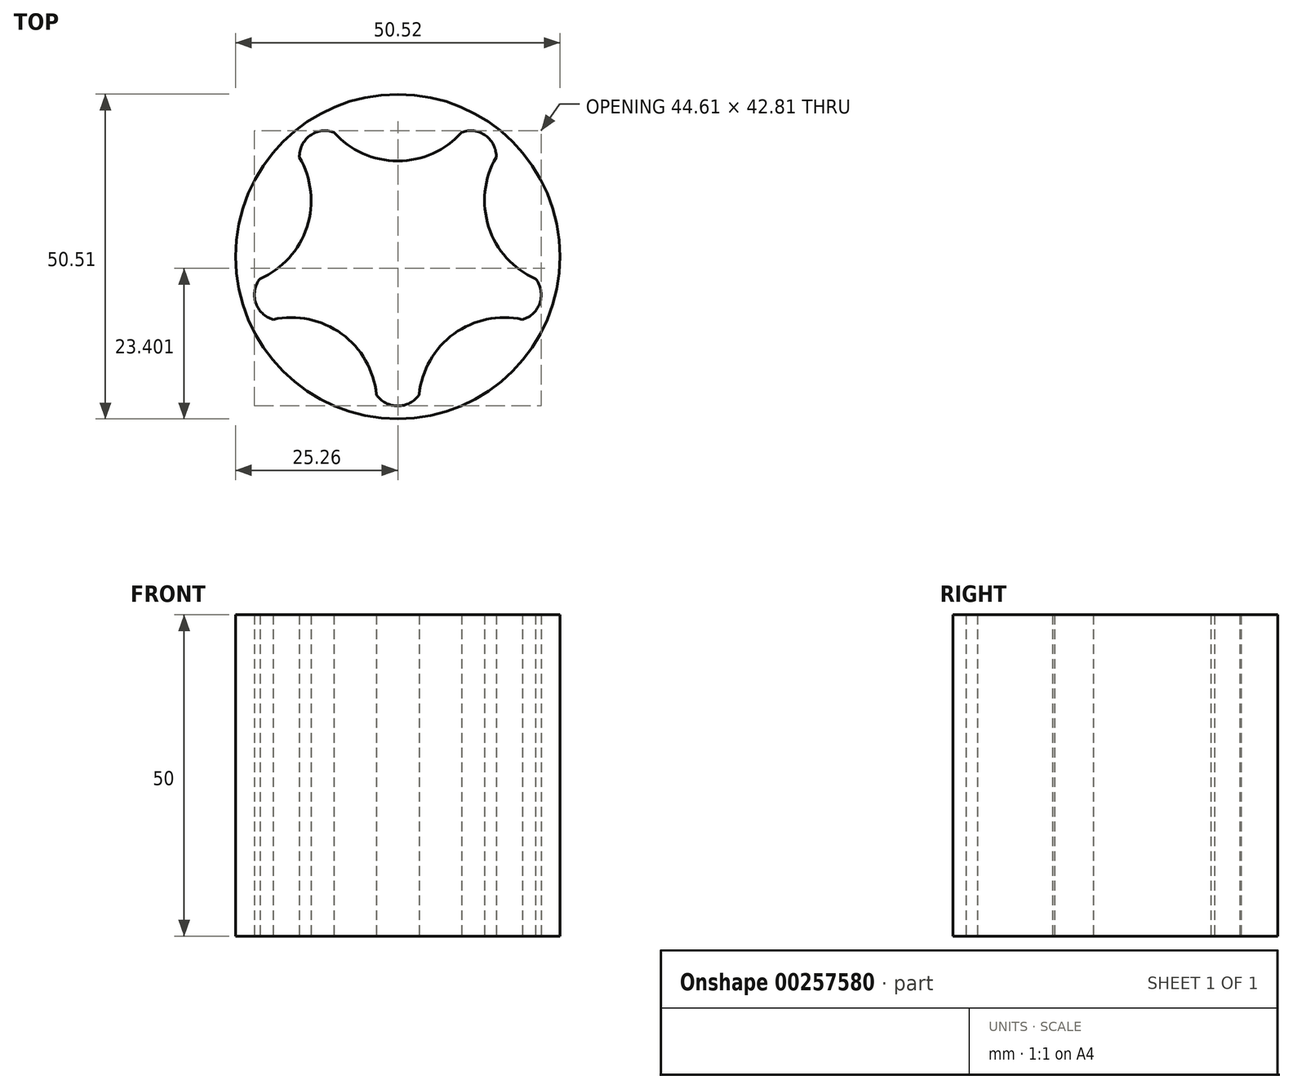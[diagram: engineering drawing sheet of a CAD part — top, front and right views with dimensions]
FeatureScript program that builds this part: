
annotation { "Feature Type Name" : "Feature", "Feature Type Description" : "" }
export const myFeature = defineFeature(function(context is Context, id is Id, definition is map)
    precondition{}
    {
        {
            var Q0;
            Q0=qCreatedBy(makeId("Top.planeOp"),FACE);
            var sketch = newSketch(context, id + "F0", { "sketchPlane" : qUnion([Q0])});
            skPoint(sketch, "E0", {"position": v(0, 16.5) * mm});
            skArc(sketch, "E1", {"start": v(3.5, 16.5) * mm, "mid": v(7.95, 7.95) * mm, "end": v(16.5, 3.5) * mm});
            skArc(sketch, "E2.MirrorCS", {"start": v(3.5, -16.5) * mm, "mid": v(7.95, -7.95) * mm, "end": v(16.5, -3.5) * mm});
            skArc(sketch, "E3.MirrorCS", {"start": v(-3.5, 16.5) * mm, "mid": v(-7.95, 7.95) * mm, "end": v(-16.5, 3.5) * mm});
            skArc(sketch, "E4.MirrorCS", {"start": v(-3.5, -16.5) * mm, "mid": v(-7.95, -7.95) * mm, "end": v(-16.5, -3.5) * mm});
            skArc(sketch, "E5", {"start": v(3.5, 16.5) * mm, "mid": v(0, 18.56) * mm, "end": v(-3.5, 16.5) * mm});
            skArc(sketch, "E6.MirrorCS", {"start": v(3.5, -16.5) * mm, "mid": v(0, -18.56) * mm, "end": v(-3.5, -16.5) * mm});
            skArc(sketch, "E7", {"start": v(16.5, -3.5) * mm, "mid": v(18.56, 0) * mm, "end": v(16.5, 3.5) * mm});
            skArc(sketch, "E8.MirrorCS", {"start": v(-16.5, -3.5) * mm, "mid": v(-18.56, 0) * mm, "end": v(-16.5, 3.5) * mm});
            skPoint(sketch, "E9", {"position": v(0, 0) * mm});
            skArc(sketch, "E10", {"start": v(14.14, 16.52) * mm, "mid": v(11.24, 7.33) * mm, "end": v(14.14, -1.87) * mm});
            skArc(sketch, "E11.MirrorCS", {"start": v(-9.2, -6.82) * mm, "mid": v(0, -3.91) * mm, "end": v(9.2, -6.82) * mm});
            skArc(sketch, "E12.MirrorCS", {"start": v(9.2, 21.47) * mm, "mid": v(0, 18.56) * mm, "end": v(-9.2, 21.47) * mm});
            skArc(sketch, "E13.MirrorCS", {"start": v(-14.14, -1.87) * mm, "mid": v(-11.24, 7.33) * mm, "end": v(-14.14, 16.52) * mm});
            skArc(sketch, "E14", {"start": v(14.14, 16.52) * mm, "mid": v(13.13, 20.45) * mm, "end": v(9.2, 21.47) * mm});
            skArc(sketch, "E15.MirrorCS", {"start": v(-9.2, -6.82) * mm, "mid": v(-13.13, -5.8) * mm, "end": v(-14.14, -1.87) * mm});
            skArc(sketch, "E16", {"start": v(9.2, -6.82) * mm, "mid": v(13.13, -5.8) * mm, "end": v(14.14, -1.87) * mm});
            skArc(sketch, "E17.MirrorCS", {"start": v(-14.14, 16.52) * mm, "mid": v(-13.13, 20.45) * mm, "end": v(-9.2, 21.47) * mm});
            skPoint(sketch, "E18", {"position": v(0, 7.33) * mm});
            skSolve(sketch);
        }
        {
            var Q0;
            Q0=makeQuery(id+"F0.imprint","IMPRINT",FACE,{"disambiguationData":[TD([[makeQuery(id+"F0.imprint","IMPRINT",EDGE,{"derivedFrom":sQuery(id+"F0.wireOp",EDGE,"E1")}),-1.0]])]});
            extrude(context, id + "F1", {"entities" : qUnion([Q0]), "depth" : 1 * mm});
        }
        {
            var Q0;
            Q0 = qSketchRegion(id + "F0", true);
            extrude(context, id + "F2", {"entities" : qUnion([Q0]), "operationType" : NewBodyOperationType.ADD, "depth" : 2 * mm});
        }
        {
            var Q0;
            Q0=makeQuery(id+"F2.opExtrude","CAP_FACE",FACE,{"disambiguationData":[OSD([sQuery(id+"F0.wireOp",EDGE,"E1"),sQuery(id+"F0.wireOp",EDGE,"E2.MirrorCS"),sQuery(id+"F0.wireOp",EDGE,"E3.MirrorCS"),sQuery(id+"F0.wireOp",EDGE,"E4.MirrorCS"),sQuery(id+"F0.wireOp",EDGE,"E6.MirrorCS"),sQuery(id+"F0.wireOp",EDGE,"E7"),sQuery(id+"F0.wireOp",EDGE,"E8.MirrorCS"),sQuery(id+"F0.wireOp",EDGE,"E10"),sQuery(id+"F0.wireOp",EDGE,"E12.MirrorCS"),sQuery(id+"F0.wireOp",EDGE,"E13.MirrorCS"),sQuery(id+"F0.wireOp",EDGE,"E14"),sQuery(id+"F0.wireOp",EDGE,"E15.MirrorCS"),sQuery(id+"F0.wireOp",EDGE,"E16"),sQuery(id+"F0.wireOp",EDGE,"E17.MirrorCS")])],"isStart":false});
            var sketch = newSketch(context, id + "F3", { "sketchPlane" : qUnion([Q0])});
            skArc(sketch, "E19", {"start": v(-9.93, 23.02) * mm, "mid": v(0, 18.56) * mm, "end": v(9.93, 23.02) * mm});
            skArc(sketch, "E20.1.0", {"start": v(15.31, 19.1) * mm, "mid": v(14.14, 8.29) * mm, "end": v(21.45, 0.22) * mm});
            skArc(sketch, "E20.2.0", {"start": v(19.4, -6.11) * mm, "mid": v(8.74, -8.34) * mm, "end": v(3.33, -17.78) * mm});
            skArc(sketch, "E20.3.0", {"start": v(-3.33, -17.78) * mm, "mid": v(-8.74, -8.34) * mm, "end": v(-19.4, -6.11) * mm});
            skArc(sketch, "E20.4.0", {"start": v(-21.45, 0.22) * mm, "mid": v(-14.14, 8.29) * mm, "end": v(-15.31, 19.1) * mm});
            skPoint(sketch, "E20.center", {"position": v(0, 3.7) * mm});
            skLineSegment(sketch, "E20.anchor1", {"start": v(0, 3.7) * mm, "end": v(0, 31.85) * mm, "construction": true});
            skLineSegment(sketch, "E20.anchor2", {"start": v(0, 3.7) * mm, "end": v(-26.78, 12.4) * mm, "construction": true});
            skArc(sketch, "E21", {"start": v(-3.33, -17.78) * mm, "mid": v(0, -19.56) * mm, "end": v(3.33, -17.78) * mm});
            skArc(sketch, "E22.1.0", {"start": v(19.4, -6.11) * mm, "mid": v(22.12, -3.5) * mm, "end": v(21.45, 0.22) * mm});
            skArc(sketch, "E22.2.0", {"start": v(15.31, 19.1) * mm, "mid": v(13.67, 22.5) * mm, "end": v(9.93, 23.02) * mm});
            skArc(sketch, "E22.3.0", {"start": v(-9.93, 23.02) * mm, "mid": v(-13.67, 22.5) * mm, "end": v(-15.31, 19.1) * mm});
            skArc(sketch, "E22.4.0", {"start": v(-21.45, 0.22) * mm, "mid": v(-22.12, -3.5) * mm, "end": v(-19.4, -6.11) * mm});
            skSolve(sketch);
        }
        {
            var Q0;
            Q0=makeQuery(id+"F3.imprint","IMPRINT",FACE,{"disambiguationData":[TD([[makeQuery(id+"F3.imprint","IMPRINT",EDGE,{"derivedFrom":sQuery(id+"F3.wireOp",EDGE,"E20.4.0")}),-1.0]])]});
            var Q1;
            Q1=makeQuery(id+"F3.imprint","IMPRINT",FACE,{"disambiguationData":[TD([[makeQuery(id+"F3.imprint","IMPRINT",EDGE,{"derivedFrom":sQuery(id+"F3.wireOp",EDGE,"E20.1.0")}),-1.0]])]});
            var Q2;
            {var subQ0=sQuery(id+"F3.wireOp",EDGE,"E21");Q2=makeQuery(id+"F3.imprint","IMPRINT",FACE,{"disambiguationData":[TD([[makeQuery(id+"F3.imprint","IMPRINT",EDGE,{"derivedFrom":subQ0}),1.0]])]});}
            var Q3;
            Q3=makeQuery(id+"F3.imprint","IMPRINT",FACE,{"disambiguationData":[TD([[makeQuery(id+"F3.imprint","IMPRINT",EDGE,{"derivedFrom":makeQuery(id+"F2.opExtrude","CAP_EDGE",EDGE,{"disambiguationData":[OSD([sQuery(id+"F0.wireOp",EDGE,"E1")])],"isStart":false})}),-1.0]])]});
            var Q4;
            Q4=makeQuery(id+"F2.opExtrude","CAP_FACE",FACE,{"disambiguationData":[OSD([sQuery(id+"F0.wireOp",EDGE,"E1"),sQuery(id+"F0.wireOp",EDGE,"E2.MirrorCS"),sQuery(id+"F0.wireOp",EDGE,"E3.MirrorCS"),sQuery(id+"F0.wireOp",EDGE,"E4.MirrorCS"),sQuery(id+"F0.wireOp",EDGE,"E6.MirrorCS"),sQuery(id+"F0.wireOp",EDGE,"E7"),sQuery(id+"F0.wireOp",EDGE,"E8.MirrorCS"),sQuery(id+"F0.wireOp",EDGE,"E10"),sQuery(id+"F0.wireOp",EDGE,"E12.MirrorCS"),sQuery(id+"F0.wireOp",EDGE,"E13.MirrorCS"),sQuery(id+"F0.wireOp",EDGE,"E14"),sQuery(id+"F0.wireOp",EDGE,"E15.MirrorCS"),sQuery(id+"F0.wireOp",EDGE,"E16"),sQuery(id+"F0.wireOp",EDGE,"E17.MirrorCS")])],"isStart":false});
            extrude(context, id + "F4", {"entities" : qUnion([Q0, Q1, Q2, Q3, Q4]), "operationType" : NewBodyOperationType.ADD, "oppositeDirection" : true, "depth" : 5 * mm, "hasSecondDirection" : true, "secondDirectionOppositeDirection" : false, "secondDirectionDepth" : 30 * mm});
        }
        {
            var Q0;
            Q0=qCreatedBy(makeId("Top.planeOp"),FACE);
            var sketch = newSketch(context, id + "F5", { "sketchPlane" : qUnion([Q0])});
            skCircle(sketch, "E23", {"center": v(0, 3.7) * mm, "radius": 25.26 * mm});
            skSolve(sketch);
        }
        {
            var Q0;
            Q0=makeQuery(id+"F5.imprint","IMPRINT",FACE,{"disambiguationData":[TD([[makeQuery(id+"F5.imprint","IMPRINT",EDGE,{"derivedFrom":sQuery(id+"F5.wireOp",EDGE,"E23")}),1.0]])]});
            extrude(context, id + "F6", {"entities" : qUnion([Q0]), "operationType" : NewBodyOperationType.ADD, "depth" : 50 * mm});
        }
        {
            var Q0;
            Q0=makeQuery(id+"F4.boolean.opBoolean","MERGE",FACE,{"derivedFrom":[makeQuery(id+"F4.opExtrude","CAP_FACE",FACE,{"disambiguationData":[OSD([sQuery(id+"F0.wireOp",EDGE,"E1"),sQuery(id+"F0.wireOp",EDGE,"E2.MirrorCS"),sQuery(id+"F0.wireOp",EDGE,"E3.MirrorCS"),sQuery(id+"F0.wireOp",EDGE,"E4.MirrorCS"),sQuery(id+"F0.wireOp",EDGE,"E6.MirrorCS"),sQuery(id+"F0.wireOp",EDGE,"E7"),sQuery(id+"F0.wireOp",EDGE,"E8.MirrorCS"),sQuery(id+"F0.wireOp",EDGE,"E10"),sQuery(id+"F0.wireOp",EDGE,"E12.MirrorCS"),sQuery(id+"F0.wireOp",EDGE,"E13.MirrorCS"),sQuery(id+"F0.wireOp",EDGE,"E14"),sQuery(id+"F0.wireOp",EDGE,"E15.MirrorCS"),sQuery(id+"F0.wireOp",EDGE,"E16"),sQuery(id+"F0.wireOp",EDGE,"E17.MirrorCS")])],"isStart":false}),makeQuery(id+"F4.opExtrude","CAP_FACE",FACE,{"disambiguationData":[OSD([sQuery(id+"F3.wireOp",EDGE,"E19"),sQuery(id+"F3.wireOp",EDGE,"E20.1.0"),sQuery(id+"F3.wireOp",EDGE,"E20.2.0"),sQuery(id+"F3.wireOp",EDGE,"E20.3.0"),sQuery(id+"F3.wireOp",EDGE,"E20.4.0"),sQuery(id+"F3.wireOp",EDGE,"E21"),sQuery(id+"F3.wireOp",EDGE,"E22.1.0"),sQuery(id+"F3.wireOp",EDGE,"E22.2.0"),sQuery(id+"F3.wireOp",EDGE,"E22.3.0"),sQuery(id+"F3.wireOp",EDGE,"E22.4.0")])],"isStart":false})]});
            extrude(context, id + "F7", {"entities" : qUnion([Q0]), "operationType" : NewBodyOperationType.REMOVE, "oppositeDirection" : true, "depth" : 100 * mm});
        }
    });
